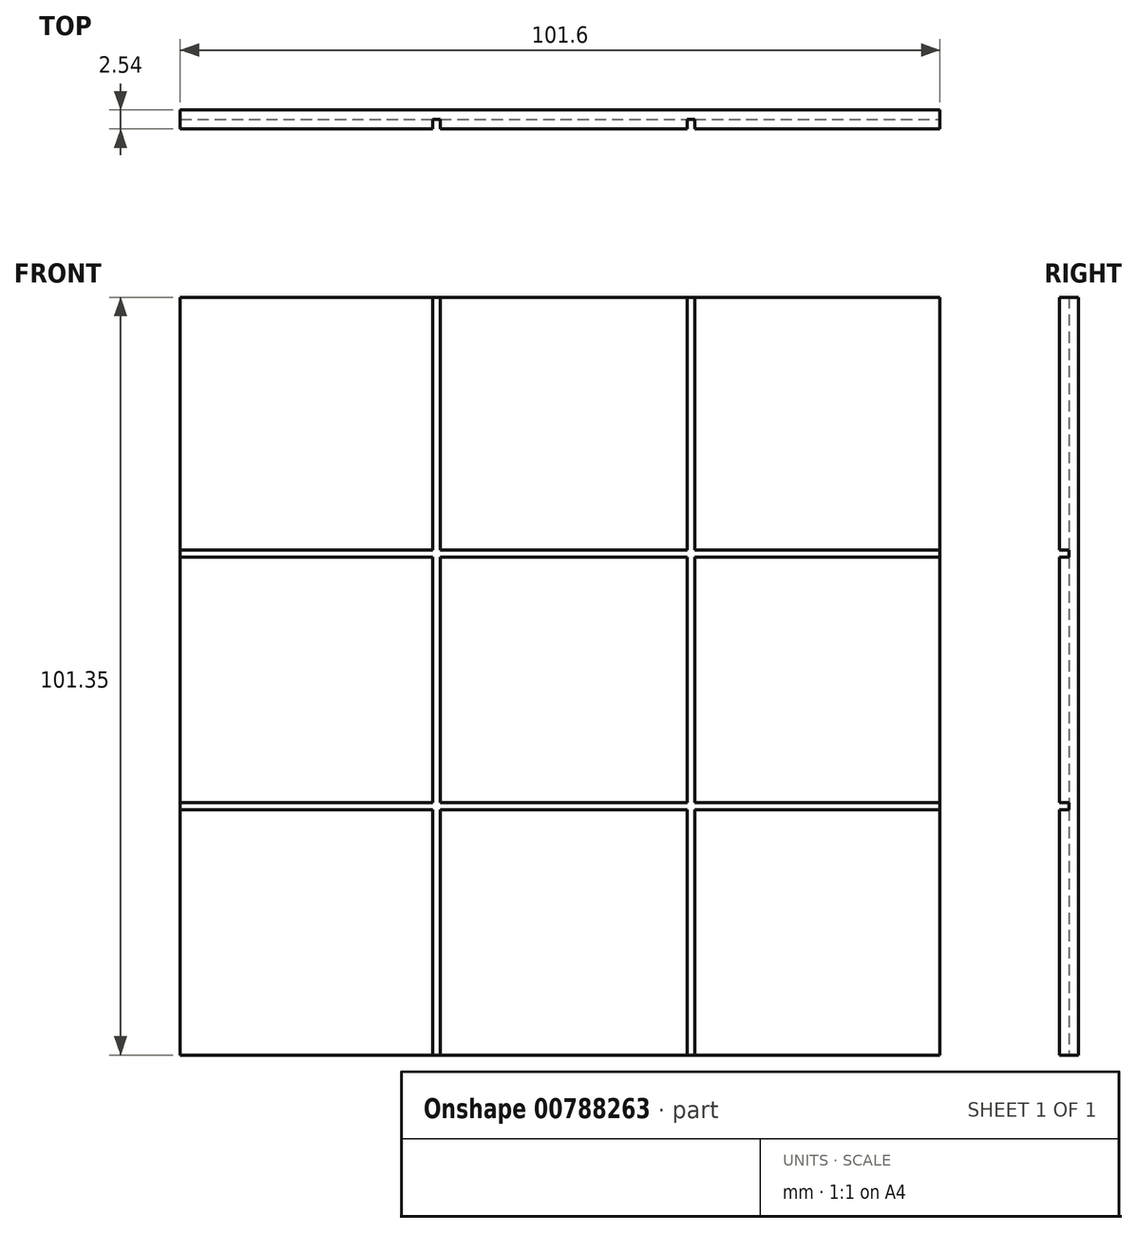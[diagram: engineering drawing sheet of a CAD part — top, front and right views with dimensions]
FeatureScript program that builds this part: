
annotation { "Feature Type Name" : "Feature", "Feature Type Description" : "" }
export const myFeature = defineFeature(function(context is Context, id is Id, definition is map)
    precondition{}
    {
        {
            var Q0;
            Q0=qCreatedBy(makeId("Front.planeOp"),FACE);
            var sketch = newSketch(context, id + "F0", { "sketchPlane" : qUnion([Q0])});
            skLineSegment(sketch, "E0.bottom", {"start": v(66.37, -22.06) * mm, "end": v(-35.23, -22.06) * mm});
            skLineSegment(sketch, "E0.top", {"start": v(66.37, 79.3) * mm, "end": v(-35.23, 79.3) * mm});
            skLineSegment(sketch, "E0.left", {"start": v(66.37, -22.06) * mm, "end": v(66.37, 79.3) * mm});
            skLineSegment(sketch, "E0.right", {"start": v(-35.23, -22.06) * mm, "end": v(-35.23, 79.3) * mm});
            skSolve(sketch);
        }
        {
            var Q0;
            Q0 = qSketchRegion(id + "F0", true);
            extrude(context, id + "F1", {"entities" : qUnion([Q0]), "depth" : 2.54 * mm, "offsetDistance" : 25.4 * mm});
        }
        {
            var Q0;
            Q0=makeQuery(id+"F1.opExtrude","CAP_FACE",FACE,{"disambiguationData":[OSD([sQuery(id+"F0.wireOp",EDGE,"E0.bottom"),sQuery(id+"F0.wireOp",EDGE,"E0.top"),sQuery(id+"F0.wireOp",EDGE,"E0.left"),sQuery(id+"F0.wireOp",EDGE,"E0.right")])],"isStart":false});
            var sketch = newSketch(context, id + "F2", { "sketchPlane" : qUnion([Q0])});
            skLineSegment(sketch, "E1", {"start": v(-35.23, 45.5) * mm, "end": v(-1.45, 45.5) * mm});
            skLineSegment(sketch, "E2", {"start": v(-35.23, 11.73) * mm, "end": v(-1.45, 11.73) * mm});
            skLineSegment(sketch, "E3", {"start": v(-1.45, 79.3) * mm, "end": v(-1.45, 45.5) * mm});
            skLineSegment(sketch, "E4", {"start": v(32.59, 79.3) * mm, "end": v(32.59, 45.5) * mm});
            skLineSegment(sketch, "E5", {"start": v(-35.23, 44.53) * mm, "end": v(-1.45, 44.53) * mm});
            skLineSegment(sketch, "E6", {"start": v(-35.23, 10.76) * mm, "end": v(-1.45, 10.76) * mm});
            skLineSegment(sketch, "E7", {"start": v(-0.48, 79.3) * mm, "end": v(-0.48, 79.17) * mm});
            skLineSegment(sketch, "E8", {"start": v(-0.48, 79.17) * mm, "end": v(-0.48, 45.5) * mm});
            skLineSegment(sketch, "E9.trimOffspring", {"start": v(-0.48, 10.76) * mm, "end": v(-0.48, -22.06) * mm});
            skLineSegment(sketch, "E10.trimOffspring", {"start": v(-1.45, 10.76) * mm, "end": v(-1.45, -22.06) * mm});
            skLineSegment(sketch, "E11.trimOffspring", {"start": v(-0.48, 11.73) * mm, "end": v(32.59, 11.73) * mm});
            skLineSegment(sketch, "E12.trimOffspring", {"start": v(-0.48, 10.76) * mm, "end": v(32.59, 10.76) * mm});
            skLineSegment(sketch, "E13.trimOffspring", {"start": v(-0.48, 45.5) * mm, "end": v(32.59, 45.5) * mm});
            skLineSegment(sketch, "E14.trimOffspring", {"start": v(-0.48, 44.53) * mm, "end": v(32.59, 44.53) * mm});
            skLineSegment(sketch, "E15.trimOffspring", {"start": v(-0.48, 44.53) * mm, "end": v(-0.48, 11.73) * mm});
            skLineSegment(sketch, "E16.trimOffspring", {"start": v(-1.45, 44.53) * mm, "end": v(-1.45, 11.73) * mm});
            skLineSegment(sketch, "E17", {"start": v(33.55, 79.3) * mm, "end": v(33.55, 76.06) * mm});
            skLineSegment(sketch, "E18", {"start": v(33.55, 76.06) * mm, "end": v(33.55, 45.5) * mm});
            skLineSegment(sketch, "E19.trimOffspring", {"start": v(33.55, 45.5) * mm, "end": v(66.37, 45.5) * mm});
            skLineSegment(sketch, "E20.trimOffspring", {"start": v(32.59, 44.53) * mm, "end": v(32.59, 11.73) * mm});
            skLineSegment(sketch, "E21.trimOffspring", {"start": v(33.55, 44.53) * mm, "end": v(66.37, 44.53) * mm});
            skLineSegment(sketch, "E22.trimOffspring", {"start": v(33.55, 44.53) * mm, "end": v(33.55, 11.73) * mm});
            skLineSegment(sketch, "E23.trimOffspring", {"start": v(33.55, 11.73) * mm, "end": v(66.37, 11.73) * mm});
            skLineSegment(sketch, "E24.trimOffspring", {"start": v(32.59, 10.76) * mm, "end": v(32.59, -22.06) * mm});
            skLineSegment(sketch, "E25.trimOffspring", {"start": v(33.55, 10.76) * mm, "end": v(33.55, -22.06) * mm});
            skLineSegment(sketch, "E26.trimOffspring", {"start": v(33.55, 10.76) * mm, "end": v(66.37, 10.76) * mm});
            skSolve(sketch);
        }
        {
            var Q0;
            {var subQ6=sQuery(id+"F2.wireOp",EDGE,"E1");Q0=makeQuery(id+"F2.imprint","IMPRINT",FACE,{"disambiguationData":[TD([[makeQuery(id+"F2.imprint","IMPRINT",EDGE,{"derivedFrom":subQ6}),-1.0]])]});}
            extrude(context, id + "F3", {"entities" : qUnion([Q0]), "operationType" : NewBodyOperationType.REMOVE, "oppositeDirection" : true, "depth" : 1.27 * mm, "offsetDistance" : 25.4 * mm});
        }
    });
